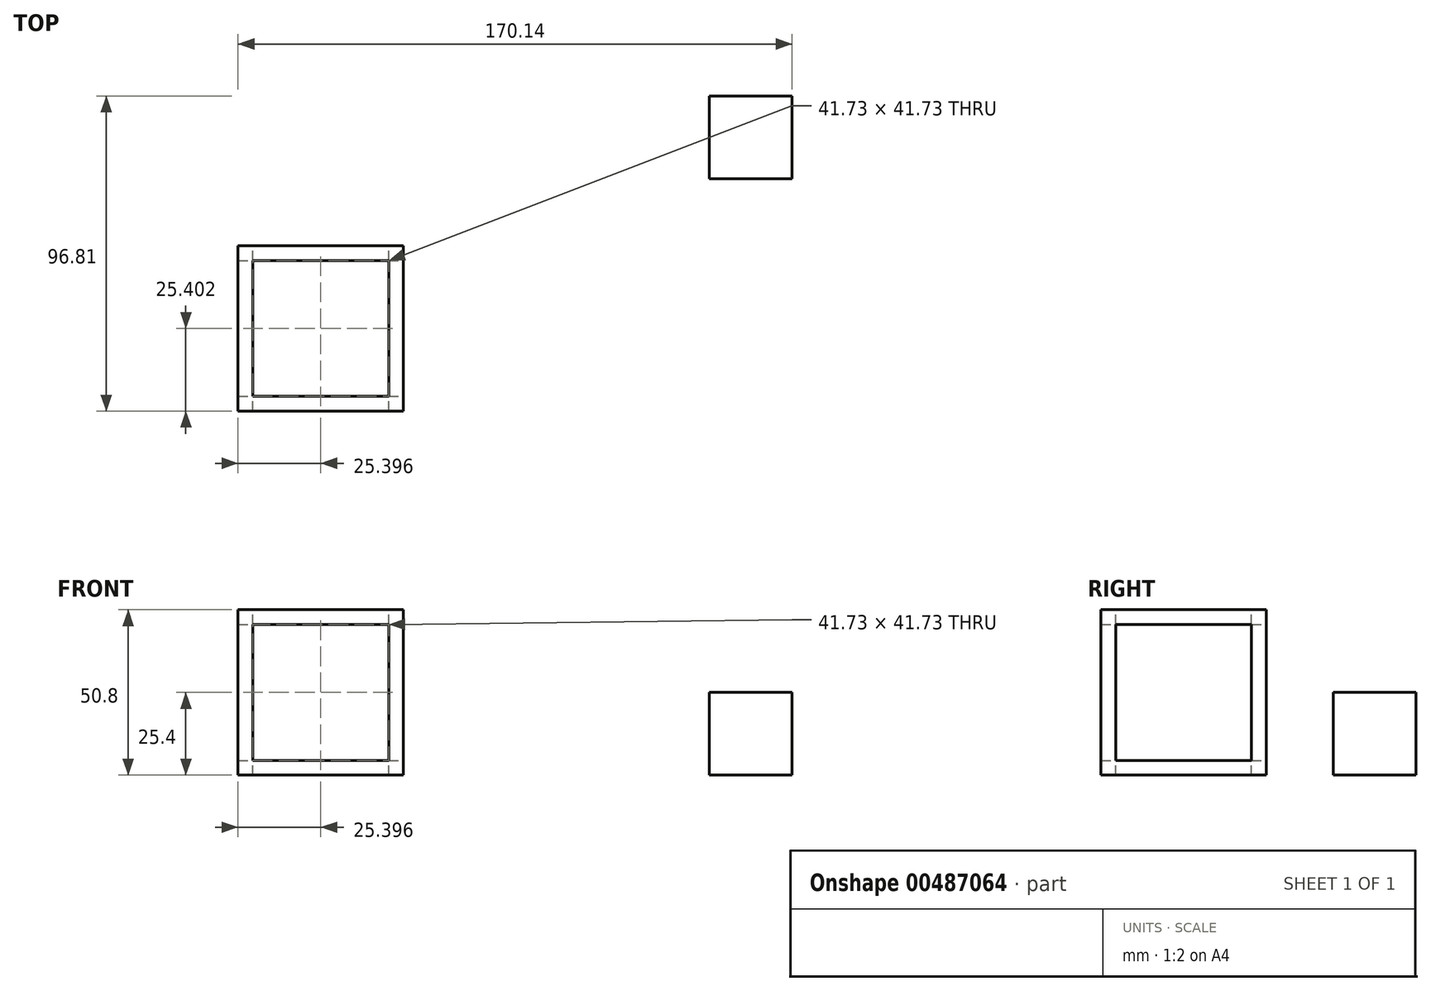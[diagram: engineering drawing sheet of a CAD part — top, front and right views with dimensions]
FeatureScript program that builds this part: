
annotation { "Feature Type Name" : "Feature", "Feature Type Description" : "" }
export const myFeature = defineFeature(function(context is Context, id is Id, definition is map)
    precondition{}
    {
        {
            var Q0;
            Q0=qCreatedBy(makeId("Top.planeOp"),FACE);
            var sketch = newSketch(context, id + "F0", { "sketchPlane" : qUnion([Q0])});
            skLineSegment(sketch, "E0.bottom", {"start": v(-75.55, -25.65) * mm, "end": v(-100.95, -25.65) * mm});
            skLineSegment(sketch, "E0.top", {"start": v(-75.55, -51.05) * mm, "end": v(-100.95, -51.05) * mm});
            skLineSegment(sketch, "E0.left", {"start": v(-75.55, -25.65) * mm, "end": v(-75.55, -51.05) * mm});
            skLineSegment(sketch, "E0.right", {"start": v(-100.95, -25.65) * mm, "end": v(-100.95, -51.05) * mm});
            skPoint(sketch, "E0.middle", {"position": v(-88.25, -38.35) * mm});
            skSolve(sketch);
        }
        {
            var Q0;
            Q0=makeQuery(id+"F0.imprint","IMPRINT",FACE,{"disambiguationData":[TD([[makeQuery(id+"F0.imprint","IMPRINT",EDGE,{"derivedFrom":sQuery(id+"F0.wireOp",EDGE,"E0.bottom")}),1.0]])]});
            extrude(context, id + "F1", {"entities" : qUnion([Q0]), "depth" : 25.4 * mm});
        }
        {
            var Q0;
            Q0=qCreatedBy(makeId("Top.planeOp"),FACE);
            var sketch = newSketch(context, id + "F2", { "sketchPlane" : qUnion([Q0])});
            skLineSegment(sketch, "E1.bottom", {"start": v(-194.9, -71.66) * mm, "end": v(-245.7, -71.66) * mm});
            skLineSegment(sketch, "E1.top", {"start": v(-194.9, -122.46) * mm, "end": v(-245.7, -122.46) * mm});
            skLineSegment(sketch, "E1.left", {"start": v(-194.9, -71.66) * mm, "end": v(-194.9, -122.46) * mm});
            skLineSegment(sketch, "E1.right", {"start": v(-245.7, -71.66) * mm, "end": v(-245.7, -122.46) * mm});
            skPoint(sketch, "E1.middle", {"position": v(-220.3, -97.06) * mm});
            skSolve(sketch);
        }
        {
            var Q0;
            Q0=makeQuery(id+"F2.imprint","IMPRINT",FACE,{"disambiguationData":[TD([[makeQuery(id+"F2.imprint","IMPRINT",EDGE,{"derivedFrom":sQuery(id+"F2.wireOp",EDGE,"E1.bottom")}),1.0]])]});
            extrude(context, id + "F3", {"entities" : qUnion([Q0]), "depth" : 50.8 * mm});
        }
        {
            var Q0;
            Q0=makeQuery(id+"F3.opExtrude","CAP_FACE",FACE,{"disambiguationData":[OSD([sQuery(id+"F2.wireOp",EDGE,"E1.bottom"),sQuery(id+"F2.wireOp",EDGE,"E1.top"),sQuery(id+"F2.wireOp",EDGE,"E1.left"),sQuery(id+"F2.wireOp",EDGE,"E1.right")])],"isStart":false});
            var sketch = newSketch(context, id + "F4", { "sketchPlane" : qUnion([Q0])});
            skLineSegment(sketch, "E2.bottom", {"start": v(-199.43, -117.92) * mm, "end": v(-241.16, -117.92) * mm});
            skLineSegment(sketch, "E2.top", {"start": v(-199.43, -76.2) * mm, "end": v(-241.16, -76.2) * mm});
            skLineSegment(sketch, "E2.left", {"start": v(-199.43, -117.92) * mm, "end": v(-199.43, -76.2) * mm});
            skLineSegment(sketch, "E2.right", {"start": v(-241.16, -117.92) * mm, "end": v(-241.16, -76.2) * mm});
            skPoint(sketch, "E2.middle", {"position": v(-220.3, -97.06) * mm});
            skSolve(sketch);
        }
        {
            var Q0;
            Q0=makeQuery(id+"F4.imprint","IMPRINT",FACE,{"disambiguationData":[TD([[makeQuery(id+"F4.imprint","IMPRINT",EDGE,{"derivedFrom":sQuery(id+"F4.wireOp",EDGE,"E2.bottom")}),-1.0]])]});
            extrude(context, id + "F5", {"entities" : qUnion([Q0]), "operationType" : NewBodyOperationType.REMOVE, "oppositeDirection" : true, "depth" : 56.13 * mm});
        }
        {
            var Q0;
            Q0=makeQuery(id+"F3.opExtrude","SWEPT_FACE",FACE,{"disambiguationData":[OSD([sQuery(id+"F2.wireOp",EDGE,"E1.bottom")])]});
            var sketch = newSketch(context, id + "F6", { "sketchPlane" : qUnion([Q0])});
            skLineSegment(sketch, "E3.bottom", {"start": v(199.43, 4.54) * mm, "end": v(241.16, 4.54) * mm});
            skLineSegment(sketch, "E3.top", {"start": v(199.43, 46.26) * mm, "end": v(241.16, 46.26) * mm});
            skLineSegment(sketch, "E3.left", {"start": v(199.43, 4.54) * mm, "end": v(199.43, 46.26) * mm});
            skLineSegment(sketch, "E3.right", {"start": v(241.16, 4.54) * mm, "end": v(241.16, 46.26) * mm});
            skPoint(sketch, "E3.middle", {"position": v(220.3, 25.4) * mm});
            skSolve(sketch);
        }
        {
            var Q0;
            Q0=makeQuery(id+"F6.imprint","IMPRINT",FACE,{"disambiguationData":[TD([[makeQuery(id+"F6.imprint","IMPRINT",EDGE,{"derivedFrom":sQuery(id+"F6.wireOp",EDGE,"E3.bottom")}),1.0]])]});
            extrude(context, id + "F7", {"entities" : qUnion([Q0]), "operationType" : NewBodyOperationType.REMOVE, "oppositeDirection" : true, "depth" : 116.6 * mm});
        }
        {
            var Q0;
            Q0=makeQuery(id+"F3.opExtrude","SWEPT_FACE",FACE,{"disambiguationData":[OSD([sQuery(id+"F2.wireOp",EDGE,"E1.left")])]});
            var sketch = newSketch(context, id + "F8", { "sketchPlane" : qUnion([Q0])});
            skLineSegment(sketch, "E4.bottom", {"start": v(-117.92, 4.54) * mm, "end": v(-76.2, 4.54) * mm});
            skLineSegment(sketch, "E4.top", {"start": v(-117.92, 46.26) * mm, "end": v(-76.2, 46.26) * mm});
            skLineSegment(sketch, "E4.left", {"start": v(-117.92, 4.54) * mm, "end": v(-117.92, 46.26) * mm});
            skLineSegment(sketch, "E4.right", {"start": v(-76.2, 4.54) * mm, "end": v(-76.2, 46.26) * mm});
            skPoint(sketch, "E4.middle", {"position": v(-97.06, 25.4) * mm});
            skSolve(sketch);
        }
        {
            var Q0;
            Q0 = qSketchRegion(id + "F8", true);
            var Q1;
            Q1=makeQuery(id+"F8.imprint","IMPRINT",FACE,{"disambiguationData":[TD([[makeQuery(id+"F8.imprint","IMPRINT",EDGE,{"derivedFrom":sQuery(id+"F8.wireOp",EDGE,"E4.bottom")}),1.0]])]});
            extrude(context, id + "F9", {"entities" : qUnion([Q0, Q1]), "operationType" : NewBodyOperationType.REMOVE, "oppositeDirection" : true, "depth" : 113.8 * mm});
        }
    });
